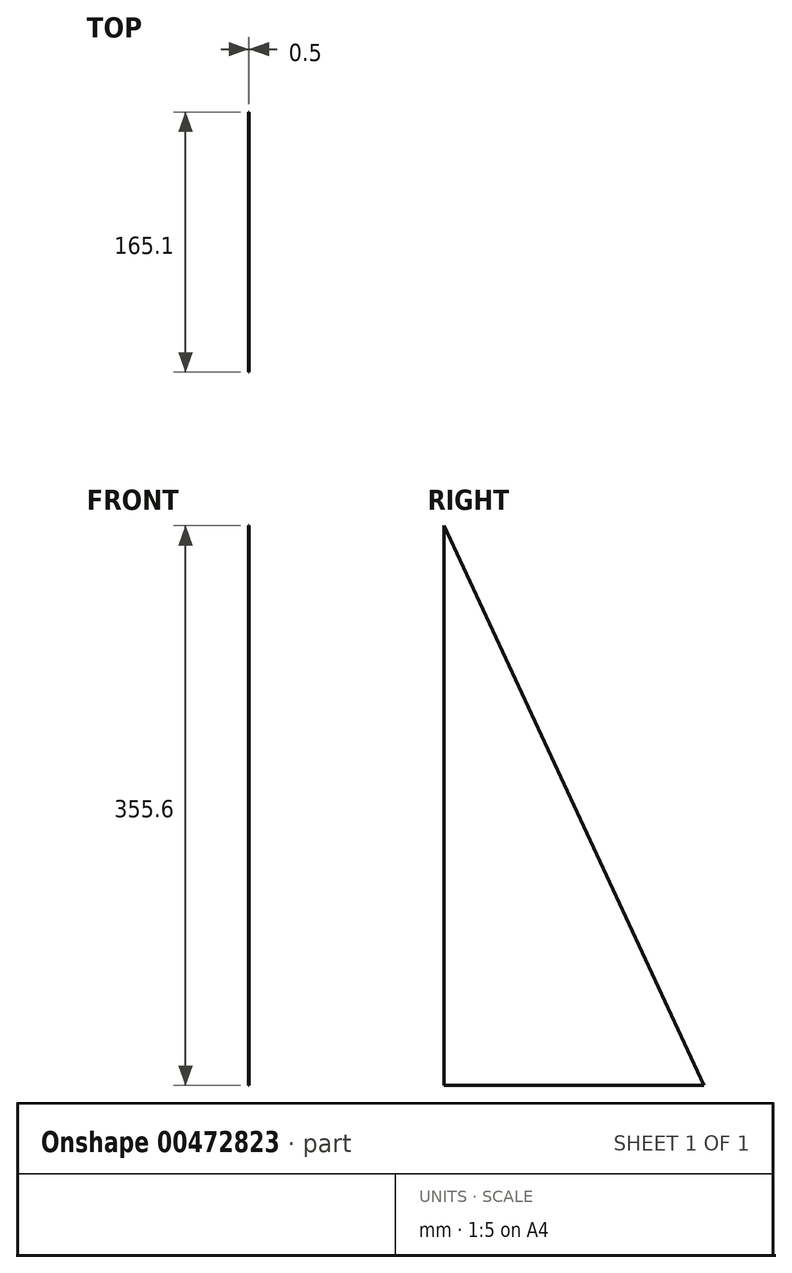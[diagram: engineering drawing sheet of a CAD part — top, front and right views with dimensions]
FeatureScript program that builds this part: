
annotation { "Feature Type Name" : "Feature", "Feature Type Description" : "" }
export const myFeature = defineFeature(function(context is Context, id is Id, definition is map)
    precondition{}
    {
        {
            assignVariable(context, id + "F0", {"name" : "Thick", "anyValue" : .5});
        }
        {
            var Q0;
            Q0=qCreatedBy(makeId("Right.planeOp"),FACE);
            var sketch = newSketch(context, id + "F1", { "sketchPlane" : qUnion([Q0])});
            skLineSegment(sketch, "E0", {"start": v(0, -4) * mm, "end": v(165.1, -4) * mm});
            skLineSegment(sketch, "E1", {"start": v(165.1, -4) * mm, "end": v(0, 351.6) * mm});
            skLineSegment(sketch, "E2", {"start": v(0, 351.6) * mm, "end": v(0, -4) * mm});
            skSolve(sketch);
        }
        {
            var Q0;
            Q0=makeQuery(id+"F1.imprint","IMPRINT",FACE,{"disambiguationData":[TD([[makeQuery(id+"F1.imprint","IMPRINT",EDGE,{"derivedFrom":sQuery(id+"F1.wireOp",EDGE,"E0")}),1.0]])]});
            extrude(context, id + "F2", {"entities" : qUnion([Q0]), "depth" : (getVariable(context, 'Thick')) * mm, "offsetDistance" : 25.4 * mm});
        }
    });
